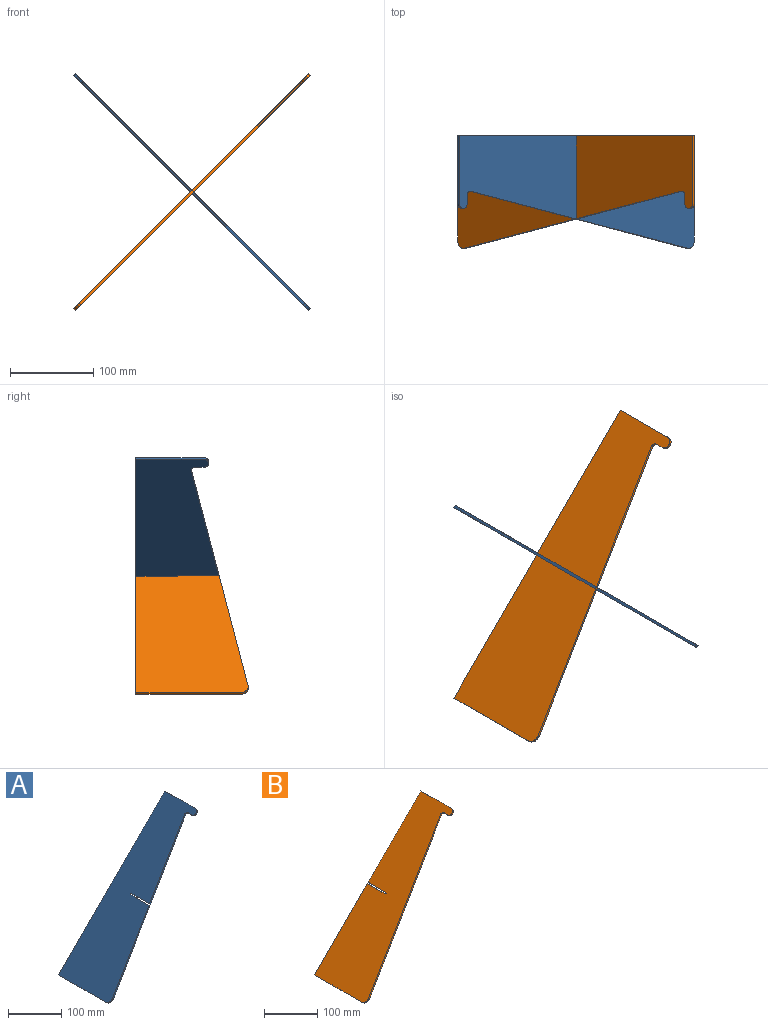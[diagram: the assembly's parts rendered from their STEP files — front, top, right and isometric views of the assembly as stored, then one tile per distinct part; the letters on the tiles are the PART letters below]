
ASSEMBLY  parts=2 mates=1
PART A: 14 faces, bbox 285x135x285 mm
  f0: plane 134.12x134.12mm, normal (0.13,-0.98,0.13), area 569.6mm2, adj f1,f9,f10,f12
  f1: cylinder r=10mm len=10.48mm, axis (0.71,0,-0.71), area 52.6mm2, adj f0,f8,f9,f10
  f2: plane 128.53x128.53mm, normal (0.13,-0.98,0.13), area 545.4mm2, adj f3,f9,f10,f13
  f3: cylinder r=5mm len=6.3mm, axis (0.71,0,-0.71), area 26.3mm2, adj f2,f4,f9,f10
  f4: plane 9.24x2.12mm, normal (-0.71,0,-0.71), area 27.7mm2, adj f3,f5,f9,f10
  f5: cylinder r=6.91mm len=11.89mm, axis (0.71,0,-0.71), area 65.1mm2, adj f4,f6,f9,f10
  f6: plane 80.79x2.12mm, normal (0.71,0,0.71), area 242.4mm2, adj f5,f7,f9,f10
  f7: plane 284.96x284.96mm, normal (0,1,0), area 1200mm2, adj f6,f8,f9,f10
  f8: plane 125x2.12mm, normal (-0.71,0,-0.71), area 375mm2, adj f1,f7,f9,f10
  f9: plane 282.84x282.84mm, normal (-0.71,0,0.71), area 40129.1mm2, adj f0,f1,f2,f3,f4,f5,f6,f7
  f10: plane 282.84x282.84mm, normal (0.71,0,-0.71), area 40129.1mm2, adj f0,f1,f2,f3,f4,f5,f6,f7
  f11: plane 4.24x4.24mm, normal (0,-1,0), area 9mm2, adj f9,f10,f12,f13
  f12: plane 50.28x2.12mm, normal (0.71,0,0.71), area 150.8mm2, adj f0,f9,f10,f11
  f13: plane 49.72x2.12mm, normal (-0.71,0,-0.71), area 149.2mm2, adj f2,f9,f10,f11
PART B: 14 faces, bbox 285x135x285 mm
  f0: plane 142.48x142.48mm, normal (0,1,0), area 595.5mm2, adj f1,f2,f10,f11
  f1: plane 282.84x282.84mm, normal (0.71,0,-0.71), area 40129.1mm2, adj f0,f3,f4,f5,f6,f7,f8,f9
  f2: plane 282.84x282.84mm, normal (-0.71,0,0.71), area 40129.1mm2, adj f0,f3,f4,f5,f6,f7,f8,f9
  f3: cylinder r=10mm len=10.48mm, axis (-0.71,0,0.71), area 52.6mm2, adj f1,f2,f4,f10
  f4: plane 262.66x262.66mm, normal (0.13,-0.98,0.13), area 1124.1mm2, adj f1,f2,f3,f5
  f5: cylinder r=5mm len=6.3mm, axis (-0.71,0,0.71), area 26.3mm2, adj f1,f2,f4,f6
  f6: plane 9.24x2.12mm, normal (-0.71,0,-0.71), area 27.7mm2, adj f1,f2,f5,f7
  f7: cylinder r=6.91mm len=11.89mm, axis (-0.71,0,0.71), area 65.1mm2, adj f1,f2,f6,f8
  f8: plane 80.79x2.12mm, normal (0.71,0,0.71), area 242.4mm2, adj f1,f2,f7,f9
  f9: plane 142.48x142.48mm, normal (0,1,0), area 595.5mm2, adj f1,f2,f8,f13
  f10: plane 125x2.12mm, normal (-0.71,0,-0.71), area 375mm2, adj f0,f1,f2,f3
  f11: plane 50x2.12mm, normal (0.71,0,0.71), area 150mm2, adj f0,f1,f2,f12
  f12: plane 4.24x4.24mm, normal (0,1,0), area 9mm2, adj f1,f2,f11,f13
  f13: plane 50x2.12mm, normal (-0.71,0,-0.71), area 150mm2, adj f1,f2,f9,f12
PLACE A rot(axis=(0,-1,0),90deg) t=(3.01,4.05,-2.93)mm
PLACE B t=(-281.95,4.05,279.92)mm
MATE revolute A.f11 <-> B.f12  axis (0,-1,0) through (1.95,2.87,-3.99)mm
